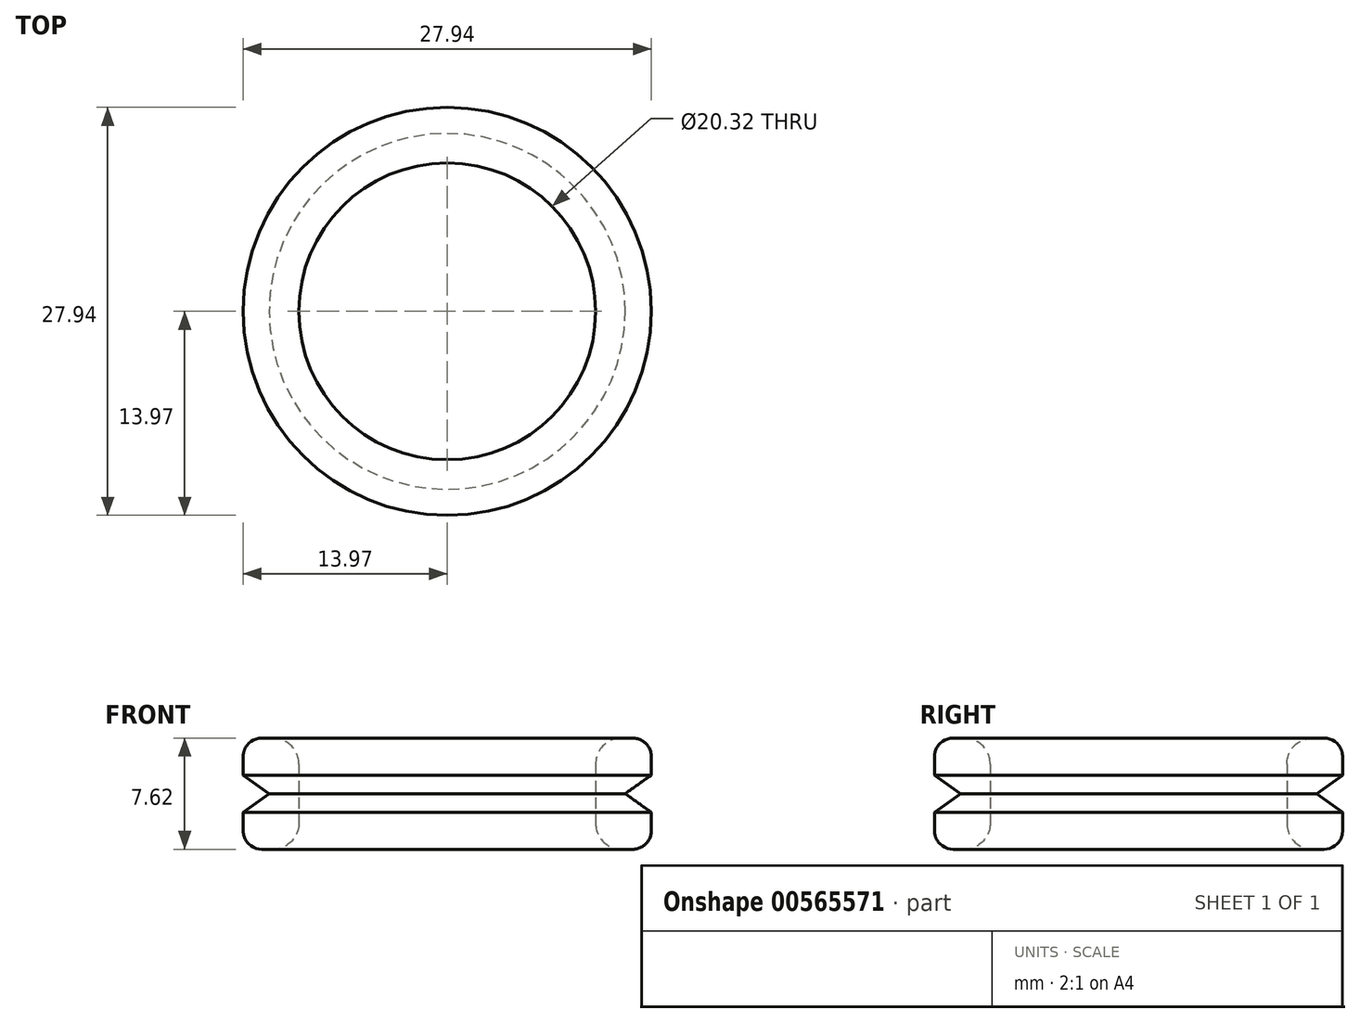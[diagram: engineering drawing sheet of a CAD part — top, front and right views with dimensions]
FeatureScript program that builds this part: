
annotation { "Feature Type Name" : "Feature", "Feature Type Description" : "" }
export const myFeature = defineFeature(function(context is Context, id is Id, definition is map)
    precondition{}
    {
        {
            var Q0;
            Q0=qCreatedBy(makeId("Top.planeOp"),FACE);
            var sketch = newSketch(context, id + "F0", { "sketchPlane" : qUnion([Q0])});
            skCircle(sketch, "E0", {"center": v(0, 0) * mm, "radius": 10.16 * mm});
            skCircle(sketch, "E1.0", {"center": v(0, 0) * mm, "radius": 13.97 * mm});
            skSolve(sketch);
        }
        {
            var Q0;
            Q0 = qSketchRegion(id + "F0", true);
            extrude(context, id + "F1", {"entities" : qUnion([Q0]), "endBound" : BoundingType.SYMMETRIC, "depth" : 7.62 * mm, "offsetDistance" : 25.4 * mm});
        }
        {
            var Q0;
            Q0=qCreatedBy(makeId("Front.planeOp"),FACE);
            var sketch = newSketch(context, id + "F2", { "sketchPlane" : qUnion([Q0])});
            skPoint(sketch, "E2", {"position": v(-13.97, 0) * mm});
            skLineSegment(sketch, "E3", {"start": v(-13.97, 0) * mm, "end": v(-13.97, 1.27) * mm});
            skLineSegment(sketch, "E4", {"start": v(-13.97, 0) * mm, "end": v(-13.97, -1.27) * mm});
            skLineSegment(sketch, "E5", {"start": v(-12.19, 0) * mm, "end": v(-13.97, 1.27) * mm});
            skLineSegment(sketch, "E6", {"start": v(-12.19, 0) * mm, "end": v(-13.97, -1.27) * mm});
            skLineSegment(sketch, "E7", {"start": v(-13.97, 1.27) * mm, "end": v(-15.12, 1.27) * mm});
            skLineSegment(sketch, "E8", {"start": v(-15.12, 1.27) * mm, "end": v(-15.12, -1.27) * mm});
            skLineSegment(sketch, "E9", {"start": v(-15.12, -1.27) * mm, "end": v(-13.97, -1.27) * mm});
            skSolve(sketch);
        }
        {
            var Q0;
            Q0 = qSketchRegion(id + "F2", true);
            var Q1;
            Q1=makeQuery(id+"F1.opExtrude","CAP_EDGE",EDGE,{"disambiguationData":[OSD([sQuery(id+"F0.wireOp",EDGE,"E1.0")])],"isStart":false});
            revolve(context, id + "F3", {"operationType" : NewBodyOperationType.REMOVE, "entities" : qUnion([Q0]), "axis" : qUnion([Q1]), "revolveType" : RevolveType.FULL, "oppositeDirection" : true});
        }
        {
            var Q0;
            Q0=makeQuery(id+"F1.opExtrude","SWEPT_FACE",FACE,{"disambiguationData":[OSD([sQuery(id+"F0.wireOp",EDGE,"E0")])]});
            fillet(context, id + "F4", {"entities" : qUnion([Q0]), "radius" : 1.78 * mm, "tangentPropagation" : true, "allowEdgeOverflow" : false});
        }
        {
            var Q0;
            Q0=makeQuery(id+"F1.opExtrude","CAP_EDGE",EDGE,{"disambiguationData":[OSD([sQuery(id+"F0.wireOp",EDGE,"E1.0")])],"isStart":false});
            var Q1;
            Q1=makeQuery(id+"F1.opExtrude","CAP_EDGE",EDGE,{"disambiguationData":[OSD([sQuery(id+"F0.wireOp",EDGE,"E1.0")])],"isStart":true});
            fillet(context, id + "F5", {"entities" : qUnion([Q0, Q1]), "radius" : 1.27 * mm, "tangentPropagation" : true, "allowEdgeOverflow" : false});
        }
        {
            var Q0;
            Q0=makeQuery(id+"F3.boolean.opBoolean","INTERSECT",EDGE,{"derivedFrom":[makeQuery(id+"F1.opExtrude","SWEPT_FACE",FACE,{"disambiguationData":[OSD([sQuery(id+"F0.wireOp",EDGE,"E1.0")])]}),makeQuery(id+"F3.opRevolve","SWEPT_FACE",FACE,{"disambiguationData":[OSD([sQuery(id+"F2.wireOp",EDGE,"E9")])]})]});
            var Q1;
            Q1=makeQuery(id+"F3.boolean.opBoolean","INTERSECT",EDGE,{"derivedFrom":[makeQuery(id+"F1.opExtrude","SWEPT_FACE",FACE,{"disambiguationData":[OSD([sQuery(id+"F0.wireOp",EDGE,"E1.0")])]}),makeQuery(id+"F3.opRevolve","SWEPT_FACE",FACE,{"disambiguationData":[OSD([sQuery(id+"F2.wireOp",EDGE,"E7")])]})]});
            fillet(context, id + "F6", {"entities" : qUnion([Q0, Q1]), "radius" : 2.3 * mm, "tangentPropagation" : true, "allowEdgeOverflow" : false});
        }
    });
